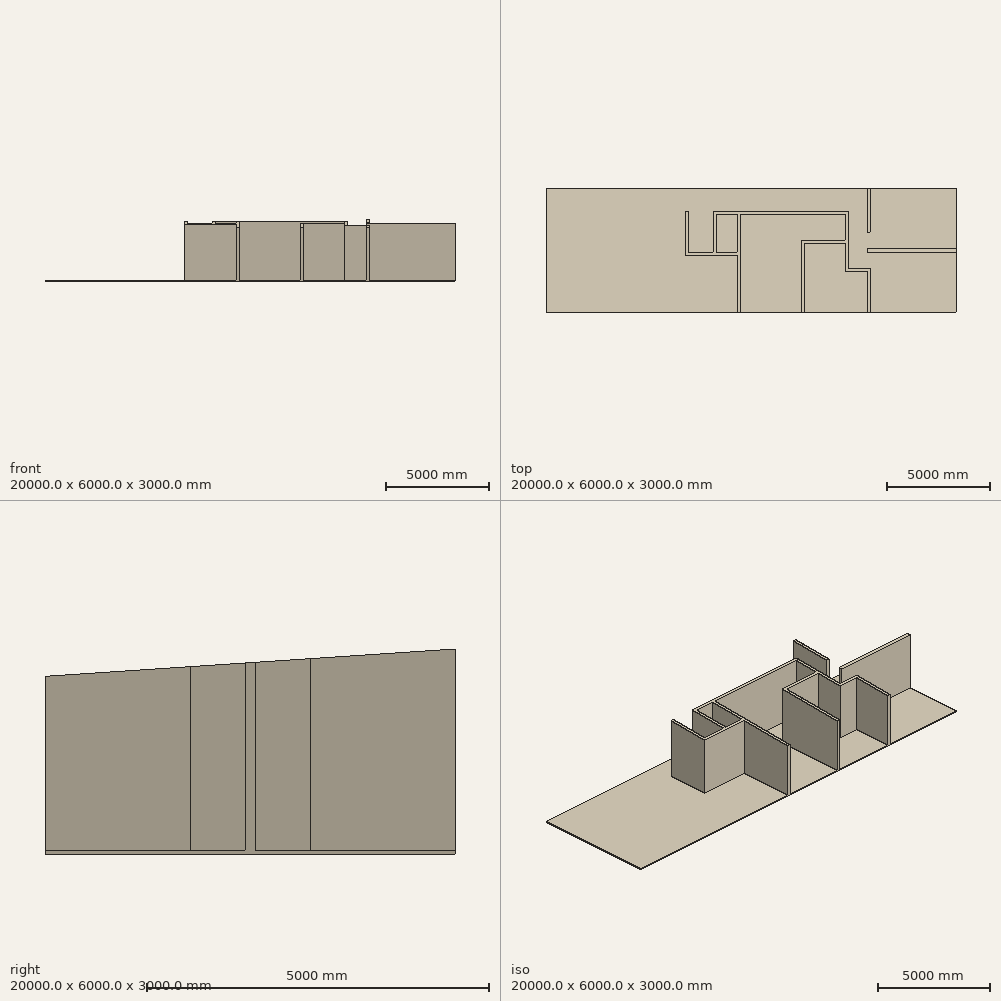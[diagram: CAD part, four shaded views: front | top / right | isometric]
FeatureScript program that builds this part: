
annotation { "Feature Type Name" : "Feature", "Feature Type Description" : "" }
export const myFeature = defineFeature(function(context is Context, id is Id, definition is map)
    precondition{}
    {
        {
            var Q0;
            Q0=qCreatedBy(makeId("Top.planeOp"),FACE);
            var sketch = newSketch(context, id + "F0", { "sketchPlane" : qUnion([Q0])});
            skLineSegment(sketch, "E0.bottom", {"start": v(-10000, 3000) * mm, "end": v(10000, 3000) * mm});
            skLineSegment(sketch, "E0.top", {"start": v(-10000, -3000) * mm, "end": v(10000, -3000) * mm});
            skLineSegment(sketch, "E0.left", {"start": v(-10000, 3000) * mm, "end": v(-10000, -3000) * mm});
            skLineSegment(sketch, "E0.right", {"start": v(10000, 3000) * mm, "end": v(10000, -3000) * mm});
            skPoint(sketch, "E0.middle", {"position": v(0, 0) * mm});
            skSolve(sketch);
        }
        {
            var Q0;
            Q0=qSketchRegion(id+"F0",true);
            extrude(context, id + "F1", {"entities" : qUnion([Q0]), "depth" : 50 * mm, "offsetDistance" : 25 * mm});
        }
        {
            var Q0;
            Q0=makeQuery(id+"F1.opExtrude","CAP_FACE",FACE,{"disambiguationData":[OSD([sQuery(id+"F0.wireOp",EDGE,"E0.bottom"),sQuery(id+"F0.wireOp",EDGE,"E0.top"),sQuery(id+"F0.wireOp",EDGE,"E0.left"),sQuery(id+"F0.wireOp",EDGE,"E0.right")])],"isStart":false});
            var sketch = newSketch(context, id + "F2", { "sketchPlane" : qUnion([Q0])});
            skLineSegment(sketch, "E1.bottom", {"start": v(10000, 75) * mm, "end": v(5650, 75) * mm});
            skLineSegment(sketch, "E1.top", {"start": v(10000, -75) * mm, "end": v(5650, -75) * mm});
            skLineSegment(sketch, "E1.left", {"start": v(10000, 75) * mm, "end": v(10000, -75) * mm});
            skLineSegment(sketch, "E1.right", {"start": v(5650, 75) * mm, "end": v(5650, -75) * mm});
            skLineSegment(sketch, "E2.bottom", {"start": v(5650, 3000) * mm, "end": v(5800, 3000) * mm});
            skLineSegment(sketch, "E2.top", {"start": v(5650, 885) * mm, "end": v(5800, 885) * mm});
            skLineSegment(sketch, "E2.left", {"start": v(5650, 3000) * mm, "end": v(5650, 885) * mm});
            skLineSegment(sketch, "E2.right", {"start": v(5800, 3000) * mm, "end": v(5800, 885) * mm});
            skLineSegment(sketch, "E3.right", {"start": v(5800, -3000) * mm, "end": v(5800, -885) * mm});
            skLineSegment(sketch, "E4.bottom", {"start": v(-1850, 1900) * mm, "end": v(4750, 1900) * mm});
            skLineSegment(sketch, "E5.left", {"start": v(4750, 1900) * mm, "end": v(4750, -885) * mm});
            skLineSegment(sketch, "E6.bottom", {"start": v(4750, -885) * mm, "end": v(5800, -885) * mm});
            skLineSegment(sketch, "E7.0", {"start": v(5650, -3000) * mm, "end": v(5650, -1035) * mm});
            skLineSegment(sketch, "E7.1", {"start": v(4600, -1035) * mm, "end": v(5650, -1035) * mm});
            skLineSegment(sketch, "E7.2", {"start": v(4600, 1750) * mm, "end": v(4600, -1035) * mm});
            skLineSegment(sketch, "E7.3", {"start": v(-1700, 1750) * mm, "end": v(-700, 1750) * mm});
            skLineSegment(sketch, "E8", {"start": v(-3200, -250) * mm, "end": v(-3200, 1900) * mm});
            skLineSegment(sketch, "E9.1", {"start": v(-3050, -100) * mm, "end": v(-3050, 1900) * mm});
            skLineSegment(sketch, "E10.bottom", {"start": v(-10000, 3000) * mm, "end": v(-7000, 3000) * mm, "construction": true});
            skLineSegment(sketch, "E10.top", {"start": v(-10000, 2300) * mm, "end": v(-7000, 2300) * mm, "construction": true});
            skLineSegment(sketch, "E10.left", {"start": v(-10000, 3000) * mm, "end": v(-10000, 2300) * mm, "construction": true});
            skLineSegment(sketch, "E10.right", {"start": v(-7000, 3000) * mm, "end": v(-7000, 2300) * mm, "construction": true});
            skLineSegment(sketch, "E11.bottom", {"start": v(-10000, 950) * mm, "end": v(-7000, 950) * mm, "construction": true});
            skLineSegment(sketch, "E11.top", {"start": v(-10000, 50) * mm, "end": v(-7000, 50) * mm, "construction": true});
            skLineSegment(sketch, "E11.left", {"start": v(-10000, 950) * mm, "end": v(-10000, 50) * mm, "construction": true});
            skLineSegment(sketch, "E11.right", {"start": v(-7000, 950) * mm, "end": v(-7000, 50) * mm, "construction": true});
            skLineSegment(sketch, "E12.bottom", {"start": v(-9500, -1150) * mm, "end": v(-7500, -1150) * mm, "construction": true});
            skLineSegment(sketch, "E12.top", {"start": v(-9500, -2050) * mm, "end": v(-7500, -2050) * mm, "construction": true});
            skLineSegment(sketch, "E12.left", {"start": v(-9500, -1150) * mm, "end": v(-9500, -2050) * mm, "construction": true});
            skLineSegment(sketch, "E12.right", {"start": v(-7500, -1150) * mm, "end": v(-7500, -2050) * mm, "construction": true});
            skLineSegment(sketch, "E13.bottom", {"start": v(-3050, 1900) * mm, "end": v(-1850, 1900) * mm, "construction": true});
            skLineSegment(sketch, "E13.top", {"start": v(-3050, -100) * mm, "end": v(-1850, -100) * mm, "construction": true});
            skLineSegment(sketch, "E13.right", {"start": v(-1850, 1750) * mm, "end": v(-1850, -100) * mm, "construction": true});
            skLineSegment(sketch, "E14", {"start": v(-3050, 1900) * mm, "end": v(-1850, -100) * mm, "construction": true});
            skLineSegment(sketch, "E15", {"start": v(-1850, 1900) * mm, "end": v(-3050, -100) * mm, "construction": true});
            skLineSegment(sketch, "E16", {"start": v(-1850, 1900) * mm, "end": v(-1850, 1750) * mm});
            skLineSegment(sketch, "E17", {"start": v(-3050, 1900) * mm, "end": v(-3200, 1900) * mm});
            skLineSegment(sketch, "E18.bottom", {"start": v(-3200, -250) * mm, "end": v(-700, -250) * mm});
            skLineSegment(sketch, "E18.top", {"start": v(-3050, -100) * mm, "end": v(-1850, -100) * mm});
            skLineSegment(sketch, "E18.left", {"start": v(-3200, -250) * mm, "end": v(-3200, -100) * mm});
            skLineSegment(sketch, "E18.right", {"start": v(-550, -250) * mm, "end": v(-550, -100) * mm});
            skLineSegment(sketch, "E19.left", {"start": v(-1850, 1750) * mm, "end": v(-1850, -100) * mm});
            skLineSegment(sketch, "E19.right", {"start": v(-1700, 1750) * mm, "end": v(-1700, -100) * mm});
            skLineSegment(sketch, "E20.top", {"start": v(-550, -3000) * mm, "end": v(-700, -3000) * mm});
            skLineSegment(sketch, "E20.left", {"start": v(-550, -250) * mm, "end": v(-550, -3000) * mm});
            skLineSegment(sketch, "E20.right", {"start": v(-700, -250) * mm, "end": v(-700, -3000) * mm});
            skLineSegment(sketch, "E21.trimOffspring", {"start": v(-1700, -100) * mm, "end": v(-700, -100) * mm});
            skLineSegment(sketch, "E22.bottom", {"start": v(4600, 500) * mm, "end": v(2450, 500) * mm});
            skLineSegment(sketch, "E22.top", {"start": v(4600, 350) * mm, "end": v(2600, 350) * mm});
            skLineSegment(sketch, "E22.left", {"start": v(4600, 500) * mm, "end": v(4600, 350) * mm});
            skLineSegment(sketch, "E22.right", {"start": v(2450, 500) * mm, "end": v(2450, 350) * mm});
            skLineSegment(sketch, "E23.top", {"start": v(2450, -3000) * mm, "end": v(2600, -3000) * mm});
            skLineSegment(sketch, "E23.left", {"start": v(2450, 350) * mm, "end": v(2450, -3000) * mm});
            skLineSegment(sketch, "E23.right", {"start": v(2600, 350) * mm, "end": v(2600, -3000) * mm});
            skLineSegment(sketch, "E24.left", {"start": v(-550, -100) * mm, "end": v(-550, 1750) * mm});
            skLineSegment(sketch, "E24.right", {"start": v(-700, -100) * mm, "end": v(-700, 1750) * mm});
            skLineSegment(sketch, "E25.trimOffspring", {"start": v(-550, 1750) * mm, "end": v(4600, 1750) * mm});
            skSolve(sketch);
        }
        {
            var Q0;
            Q0=makeQuery(id+"F2.imprint","IMPRINT",FACE,{"disambiguationData":[TD([[makeQuery(id+"F2.imprint","IMPRINT",EDGE,{"derivedFrom":sQuery(id+"F2.wireOp",EDGE,"E22.bottom")}),1.0]])]});
            var Q1;
            {var subQ0=sQuery(id+"F2.wireOp",EDGE,"E3.right");Q1=makeQuery(id+"F2.imprint","IMPRINT",FACE,{"disambiguationData":[TD([[makeQuery(id+"F2.imprint","IMPRINT",EDGE,{"derivedFrom":subQ0}),1.0]])]});}
            var Q2;
            Q2=makeQuery(id+"F2.imprint","IMPRINT",FACE,{"disambiguationData":[TD([[makeQuery(id+"F2.imprint","IMPRINT",EDGE,{"derivedFrom":sQuery(id+"F2.wireOp",EDGE,"E1.bottom")}),1.0]])]});
            var Q3;
            Q3=makeQuery(id+"F2.imprint","IMPRINT",FACE,{"disambiguationData":[TD([[makeQuery(id+"F2.imprint","IMPRINT",EDGE,{"derivedFrom":sQuery(id+"F2.wireOp",EDGE,"E2.bottom")}),-1.0]])]});
            extrude(context, id + "F3", {"entities" : qUnion([Q0, Q1, Q2, Q3]), "operationType" : NewBodyOperationType.ADD, "depth" : 3000 * mm, "offsetDistance" : 25 * mm});
        }
        {
            var Q0;
            Q0=makeQuery(id+"F1.opExtrude","SWEPT_FACE",FACE,{"disambiguationData":[OSD([sQuery(id+"F0.wireOp",EDGE,"E0.left")])]});
            var sketch = newSketch(context, id + "F4", { "sketchPlane" : qUnion([Q0])});
            skLineSegment(sketch, "E26", {"start": v(3000, 2600) * mm, "end": v(-3000, 3000) * mm});
            skLineSegment(sketch, "E27", {"start": v(-3000, 3000) * mm, "end": v(-3000, 3400) * mm});
            skLineSegment(sketch, "E28", {"start": v(-3000, 3400) * mm, "end": v(3000, 3400) * mm});
            skLineSegment(sketch, "E29", {"start": v(3000, 3400) * mm, "end": v(3000, 2600) * mm});
            skSolve(sketch);
        }
        {
            var Q0;
            Q0=makeQuery(id+"F4.imprint","IMPRINT",FACE,{"disambiguationData":[TD([[makeQuery(id+"F4.imprint","IMPRINT",EDGE,{"derivedFrom":sQuery(id+"F4.wireOp",EDGE,"E26")}),-1.0]])]});
            extrude(context, id + "F5", {"entities" : qUnion([Q0]), "operationType" : NewBodyOperationType.REMOVE, "endBound" : BoundingType.THROUGH_ALL, "oppositeDirection" : true, "depth" : 25 * mm, "offsetDistance" : 25 * mm});
        }
    });
